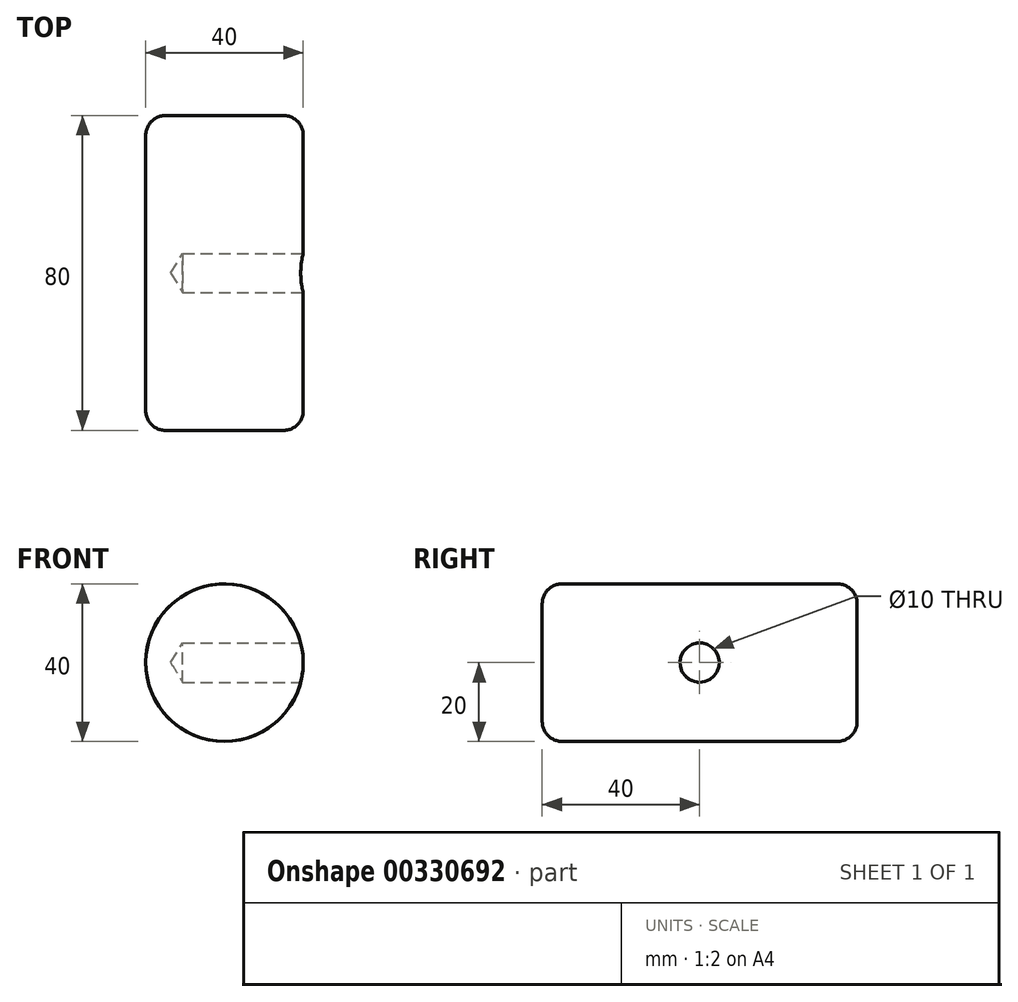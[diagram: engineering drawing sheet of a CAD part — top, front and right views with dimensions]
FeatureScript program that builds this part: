
annotation { "Feature Type Name" : "Feature", "Feature Type Description" : "" }
export const myFeature = defineFeature(function(context is Context, id is Id, definition is map)
    precondition{}
    {
        {
            var Q0;
            Q0=qCreatedBy(makeId("Front.planeOp"),FACE);
            var sketch = newSketch(context, id + "F0", { "sketchPlane" : qUnion([Q0])});
            skCircle(sketch, "E0", {"center": v(0, 0) * mm, "radius": 20 * mm});
            skSolve(sketch);
        }
        {
            var Q0;
            Q0=makeQuery(id+"F0.imprint","IMPRINT",FACE,{"disambiguationData":[TD([[makeQuery(id+"F0.imprint","IMPRINT",EDGE,{"derivedFrom":sQuery(id+"F0.wireOp",EDGE,"E0")}),1.0]])]});
            extrude(context, id + "F1", {"entities" : qUnion([Q0]), "depth" : 80 * mm});
        }
        {
            var Q0;
            Q0=qCreatedBy(makeId("Right.planeOp"),FACE);
            cPlane(context, id + "F2", {"entities" : qUnion([Q0]), "cplaneType" : CPlaneType.OFFSET, "offset" : 20 * mm, "width" : 150 * mm, "height" : 150 * mm});
        }
        {
            var Q0;
            Q0=qCreatedBy(id+"F2.planeOp",FACE);
            var sketch = newSketch(context, id + "F3", { "sketchPlane" : qUnion([Q0])});
            skPoint(sketch, "E1", {"position": v(-40, 0) * mm});
            skSolve(sketch);
        }
        {
            var Q0;
            Q0=sQuery(id+"F3.wireOp",VERTEX,"E1");
            var Q1;
            Q1=makeQuery(id+"F1.opExtrude","SWEPT_BODY",BODY,{"disambiguationData":[OSD([sQuery(id+"F0.wireOp",EDGE,"E0")])]});
            hole(context, id + "F4", {"style" : HoleStyle.SIMPLE, "endStyle" : HoleEndStyle.BLIND, "holeDiameter" : 10 * mm, "holeDepth" : 30 * mm, "tappedDepth" : 12 * mm, "tapClearance" : 3, "locations" : qUnion([Q0]), "scope" : qUnion([Q1])});
        }
        {
            var Q0;
            Q0=makeQuery(id+"F1.opExtrude","CAP_EDGE",EDGE,{"disambiguationData":[OSD([sQuery(id+"F0.wireOp",EDGE,"E0")])],"isStart":true});
            fillet(context, id + "F5", {"entities" : qUnion([Q0]), "radius" : 5 * mm, "tangentPropagation" : true, "allowEdgeOverflow" : false});
        }
        {
            var Q0;
            Q0=makeQuery(id+"F1.opExtrude","CAP_EDGE",EDGE,{"disambiguationData":[OSD([sQuery(id+"F0.wireOp",EDGE,"E0")])],"isStart":false});
            fillet(context, id + "F6", {"entities" : qUnion([Q0]), "radius" : 5 * mm, "tangentPropagation" : true, "allowEdgeOverflow" : false});
        }
    });
